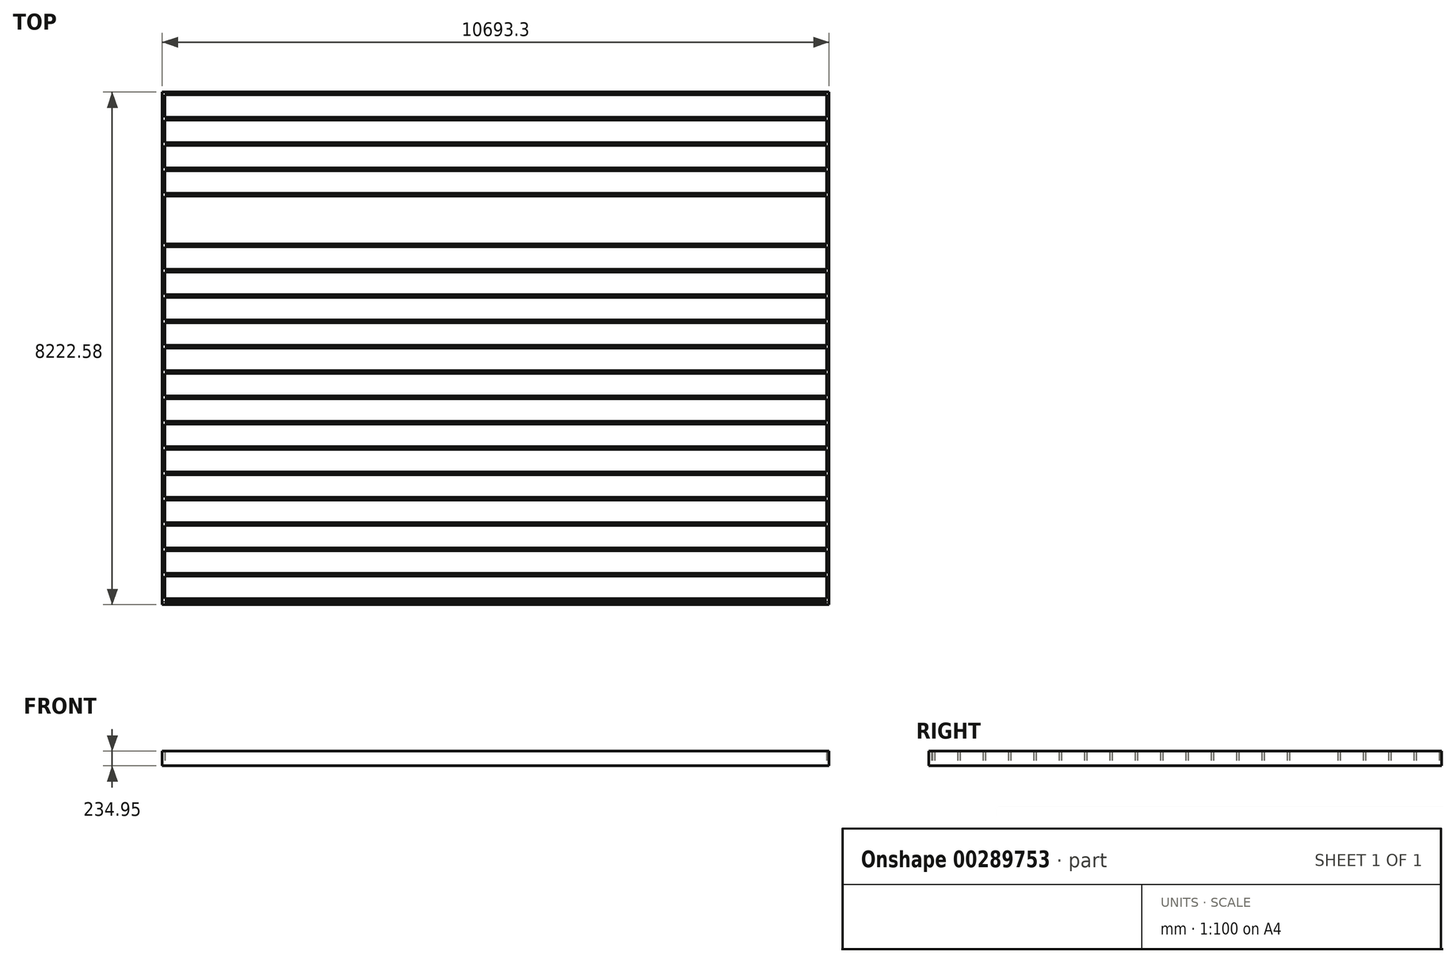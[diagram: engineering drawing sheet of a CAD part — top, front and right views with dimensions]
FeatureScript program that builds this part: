
annotation { "Feature Type Name" : "Feature", "Feature Type Description" : "" }
export const myFeature = defineFeature(function(context is Context, id is Id, definition is map)
    precondition{}
    {
        {
            var Q0;
            Q0=qCreatedBy(makeId("Top.planeOp"),FACE);
            var sketch = newSketch(context, id + "F0", { "sketchPlane" : qUnion([Q0])});
            skLineSegment(sketch, "E0.bottom", {"start": v(-5346.65, -4111.3) * mm, "end": v(5346.65, -4111.3) * mm});
            skLineSegment(sketch, "E0.top", {"start": v(-5346.65, 4111.3) * mm, "end": v(5346.65, 4111.3) * mm});
            skLineSegment(sketch, "E0.left", {"start": v(-5346.65, -4111.3) * mm, "end": v(-5346.65, 4111.3) * mm});
            skLineSegment(sketch, "E0.right", {"start": v(5346.65, -4111.3) * mm, "end": v(5346.65, 4111.3) * mm});
            skPoint(sketch, "E0.middle", {"position": v(0, 0) * mm});
            skLineSegment(sketch, "E1.bottom", {"start": v(5305.5, -4070.15) * mm, "end": v(-5305.5, -4070.15) * mm});
            skLineSegment(sketch, "E1.top", {"start": v(5305.5, 4070.15) * mm, "end": v(-5305.5, 4070.15) * mm});
            skLineSegment(sketch, "E1.left", {"start": v(5305.5, -4070.15) * mm, "end": v(5305.5, 4070.15) * mm});
            skLineSegment(sketch, "E1.right", {"start": v(-5305.5, -4070.15) * mm, "end": v(-5305.5, 4070.15) * mm});
            skLineSegment(sketch, "E2", {"start": v(-5305.5, 3704.9) * mm, "end": v(5305.5, 3704.9) * mm});
            skLineSegment(sketch, "E3", {"start": v(5305.5, 3663.75) * mm, "end": v(-5305.5, 3663.75) * mm});
            skLineSegment(sketch, "E4", {"start": v(-5305.5, 3298.5) * mm, "end": v(5305.5, 3298.5) * mm});
            skLineSegment(sketch, "E5", {"start": v(5305.5, 3257.35) * mm, "end": v(-5305.5, 3257.35) * mm});
            skLineSegment(sketch, "E6", {"start": v(-5305.5, 3277.92) * mm, "end": v(5305.5, 3277.92) * mm, "construction": true});
            skLineSegment(sketch, "E7.MirrorCS", {"start": v(5305.5, 2892.1) * mm, "end": v(-5305.5, 2892.1) * mm});
            skLineSegment(sketch, "E8.MirrorCS", {"start": v(-5305.5, 2850.95) * mm, "end": v(5305.5, 2850.95) * mm});
            skLineSegment(sketch, "E9", {"start": v(5305.5, 2871.52) * mm, "end": v(-5305.5, 2871.52) * mm, "construction": true});
            skLineSegment(sketch, "E10.MirrorCS", {"start": v(5305.5, 2485.7) * mm, "end": v(-5305.5, 2485.7) * mm});
            skLineSegment(sketch, "E11.MirrorCS", {"start": v(-5305.5, 2444.55) * mm, "end": v(5305.5, 2444.55) * mm});
            skLineSegment(sketch, "E12.MirrorCS", {"start": v(-5305.5, 2465.12) * mm, "end": v(5305.5, 2465.12) * mm, "construction": true});
            skLineSegment(sketch, "E13.MirrorCS", {"start": v(5305.5, 2079.3) * mm, "end": v(-5305.5, 2079.3) * mm});
            skLineSegment(sketch, "E14.MirrorCS", {"start": v(-5305.5, 2038.15) * mm, "end": v(5305.5, 2038.15) * mm});
            skLineSegment(sketch, "E15.MirrorCS", {"start": v(-5305.5, 2079.3) * mm, "end": v(5305.5, 2079.3) * mm});
            skLineSegment(sketch, "E16.MirrorCS", {"start": v(5305.5, 2038.15) * mm, "end": v(-5305.5, 2038.15) * mm});
            skLineSegment(sketch, "E17.MirrorCS", {"start": v(5305.5, 1672.9) * mm, "end": v(-5305.5, 1672.9) * mm});
            skLineSegment(sketch, "E18.MirrorCS", {"start": v(-5305.5, 1631.75) * mm, "end": v(5305.5, 1631.75) * mm});
            skLineSegment(sketch, "E19.MirrorCS", {"start": v(5305.5, 1266.5) * mm, "end": v(-5305.5, 1266.5) * mm});
            skLineSegment(sketch, "E20.MirrorCS", {"start": v(-5305.5, 1225.35) * mm, "end": v(5305.5, 1225.35) * mm});
            skLineSegment(sketch, "E21", {"start": v(-5305.5, 1245.92) * mm, "end": v(5305.5, 1245.92) * mm, "construction": true});
            skLineSegment(sketch, "E22.MirrorCS", {"start": v(-5305.5, 860.1) * mm, "end": v(5305.5, 860.1) * mm});
            skLineSegment(sketch, "E23.MirrorCS", {"start": v(5305.5, 818.95) * mm, "end": v(-5305.5, 818.95) * mm});
            skLineSegment(sketch, "E24.MirrorCS", {"start": v(5305.5, 453.7) * mm, "end": v(-5305.5, 453.7) * mm});
            skLineSegment(sketch, "E25.MirrorCS", {"start": v(-5305.5, 412.55) * mm, "end": v(5305.5, 412.55) * mm});
            skLineSegment(sketch, "E26.MirrorCS", {"start": v(-5305.5, 47.3) * mm, "end": v(5305.5, 47.3) * mm});
            skLineSegment(sketch, "E27.MirrorCS", {"start": v(5305.5, 6.15) * mm, "end": v(-5305.5, 6.15) * mm});
            skLineSegment(sketch, "E28.MirrorCS", {"start": v(-5305.5, -359.1) * mm, "end": v(5305.5, -359.1) * mm});
            skLineSegment(sketch, "E29.MirrorCS", {"start": v(5305.5, -400.25) * mm, "end": v(-5305.5, -400.25) * mm});
            skLineSegment(sketch, "E30.MirrorCS", {"start": v(5305.5, -765.5) * mm, "end": v(-5305.5, -765.5) * mm});
            skLineSegment(sketch, "E31.MirrorCS", {"start": v(-5305.5, -806.65) * mm, "end": v(5305.5, -806.65) * mm});
            skLineSegment(sketch, "E32.MirrorCS", {"start": v(5305.5, -1171.9) * mm, "end": v(-5305.5, -1171.9) * mm});
            skLineSegment(sketch, "E33.MirrorCS", {"start": v(-5305.5, -1213.05) * mm, "end": v(5305.5, -1213.05) * mm});
            skLineSegment(sketch, "E34", {"start": v(-5305.5, -1192.48) * mm, "end": v(5305.5, -1192.48) * mm, "construction": true});
            skLineSegment(sketch, "E35.MirrorCS", {"start": v(-5305.5, -1578.3) * mm, "end": v(5305.5, -1578.3) * mm});
            skLineSegment(sketch, "E36.MirrorCS", {"start": v(5305.5, -1619.45) * mm, "end": v(-5305.5, -1619.45) * mm});
            skLineSegment(sketch, "E37.MirrorCS", {"start": v(5305.5, -1984.7) * mm, "end": v(-5305.5, -1984.7) * mm});
            skLineSegment(sketch, "E38.MirrorCS", {"start": v(-5305.5, -2025.85) * mm, "end": v(5305.5, -2025.85) * mm});
            skLineSegment(sketch, "E39.MirrorCS", {"start": v(5305.5, -2391.1) * mm, "end": v(-5305.5, -2391.1) * mm});
            skLineSegment(sketch, "E40.MirrorCS", {"start": v(-5305.5, -2432.25) * mm, "end": v(5305.5, -2432.25) * mm});
            skLineSegment(sketch, "E41.MirrorCS", {"start": v(-5305.5, -2797.5) * mm, "end": v(5305.5, -2797.5) * mm});
            skLineSegment(sketch, "E42.MirrorCS", {"start": v(5305.5, -2838.65) * mm, "end": v(-5305.5, -2838.65) * mm});
            skLineSegment(sketch, "E43.MirrorCS", {"start": v(5305.5, -3203.9) * mm, "end": v(-5305.5, -3203.9) * mm});
            skLineSegment(sketch, "E44.MirrorCS", {"start": v(-5305.5, -3245.05) * mm, "end": v(5305.5, -3245.05) * mm});
            skLineSegment(sketch, "E45.MirrorCS", {"start": v(-5305.5, -3610.3) * mm, "end": v(5305.5, -3610.3) * mm});
            skLineSegment(sketch, "E46.MirrorCS", {"start": v(5305.5, -3651.45) * mm, "end": v(-5305.5, -3651.45) * mm});
            skLineSegment(sketch, "E47.MirrorCS", {"start": v(-5305.5, -4016.7) * mm, "end": v(5305.5, -4016.7) * mm});
            skLineSegment(sketch, "E48.MirrorCS", {"start": v(5305.5, -4057.85) * mm, "end": v(-5305.5, -4057.85) * mm});
            skLineSegment(sketch, "E49.MirrorCS", {"start": v(5305.5, -5277.05) * mm, "end": v(-5305.5, -5277.05) * mm});
            skLineSegment(sketch, "E50.MirrorCS", {"start": v(-5305.5, -5235.9) * mm, "end": v(5305.5, -5235.9) * mm});
            skLineSegment(sketch, "E51.MirrorCS", {"start": v(5305.5, -4870.65) * mm, "end": v(-5305.5, -4870.65) * mm});
            skLineSegment(sketch, "E52.MirrorCS", {"start": v(-5305.5, -4829.5) * mm, "end": v(5305.5, -4829.5) * mm});
            skLineSegment(sketch, "E53.MirrorCS", {"start": v(-5305.5, -4464.25) * mm, "end": v(5305.5, -4464.25) * mm});
            skLineSegment(sketch, "E54.MirrorCS", {"start": v(5305.5, -4423.1) * mm, "end": v(-5305.5, -4423.1) * mm});
            skSolve(sketch);
        }
        {
            var Q0;
            Q0=makeQuery(id+"F0.imprint","IMPRINT",FACE,{"disambiguationData":[TD([[makeQuery(id+"F0.imprint","IMPRINT",EDGE,{"derivedFrom":sQuery(id+"F0.wireOp",EDGE,"E0.bottom")}),1.0]])]});
            var Q1;
            {var subQ0=sQuery(id+"F0.wireOp",EDGE,"E2");Q1=makeQuery(id+"F0.imprint","IMPRINT",FACE,{"disambiguationData":[TD([[makeQuery(id+"F0.imprint","IMPRINT",EDGE,{"derivedFrom":subQ0}),-1.0]])]});}
            var Q2;
            {var subQ0=sQuery(id+"F0.wireOp",EDGE,"E4");Q2=makeQuery(id+"F0.imprint","IMPRINT",FACE,{"disambiguationData":[TD([[makeQuery(id+"F0.imprint","IMPRINT",EDGE,{"derivedFrom":subQ0}),-1.0]])]});}
            var Q3;
            {var subQ0=sQuery(id+"F0.wireOp",EDGE,"E7.MirrorCS");Q3=makeQuery(id+"F0.imprint","IMPRINT",FACE,{"disambiguationData":[TD([[makeQuery(id+"F0.imprint","IMPRINT",EDGE,{"derivedFrom":subQ0}),1.0]])]});}
            var Q4;
            {var subQ0=sQuery(id+"F0.wireOp",EDGE,"E10.MirrorCS");Q4=makeQuery(id+"F0.imprint","IMPRINT",FACE,{"disambiguationData":[TD([[makeQuery(id+"F0.imprint","IMPRINT",EDGE,{"derivedFrom":subQ0}),1.0]])]});}
            var Q5;
            {var subQ0=sQuery(id+"F0.wireOp",EDGE,"E15.MirrorCS");Q5=makeQuery(id+"F0.imprint","IMPRINT",FACE,{"disambiguationData":[TD([[makeQuery(id+"F0.imprint","IMPRINT",EDGE,{"derivedFrom":subQ0}),-1.0]])]});}
            var Q6;
            {var subQ0=sQuery(id+"F0.wireOp",EDGE,"E17.MirrorCS");Q6=makeQuery(id+"F0.imprint","IMPRINT",FACE,{"disambiguationData":[TD([[makeQuery(id+"F0.imprint","IMPRINT",EDGE,{"derivedFrom":subQ0}),1.0]])]});}
            var Q7;
            {var subQ0=sQuery(id+"F0.wireOp",EDGE,"E19.MirrorCS");Q7=makeQuery(id+"F0.imprint","IMPRINT",FACE,{"disambiguationData":[TD([[makeQuery(id+"F0.imprint","IMPRINT",EDGE,{"derivedFrom":subQ0}),1.0]])]});}
            var Q8;
            {var subQ0=sQuery(id+"F0.wireOp",EDGE,"E22.MirrorCS");Q8=makeQuery(id+"F0.imprint","IMPRINT",FACE,{"disambiguationData":[TD([[makeQuery(id+"F0.imprint","IMPRINT",EDGE,{"derivedFrom":subQ0}),-1.0]])]});}
            var Q9;
            {var subQ0=sQuery(id+"F0.wireOp",EDGE,"E24.MirrorCS");Q9=makeQuery(id+"F0.imprint","IMPRINT",FACE,{"disambiguationData":[TD([[makeQuery(id+"F0.imprint","IMPRINT",EDGE,{"derivedFrom":subQ0}),1.0]])]});}
            var Q10;
            {var subQ0=sQuery(id+"F0.wireOp",EDGE,"E26.MirrorCS");Q10=makeQuery(id+"F0.imprint","IMPRINT",FACE,{"disambiguationData":[TD([[makeQuery(id+"F0.imprint","IMPRINT",EDGE,{"derivedFrom":subQ0}),-1.0]])]});}
            var Q11;
            {var subQ0=sQuery(id+"F0.wireOp",EDGE,"E28.MirrorCS");Q11=makeQuery(id+"F0.imprint","IMPRINT",FACE,{"disambiguationData":[TD([[makeQuery(id+"F0.imprint","IMPRINT",EDGE,{"derivedFrom":subQ0}),-1.0]])]});}
            var Q12;
            {var subQ0=sQuery(id+"F0.wireOp",EDGE,"E30.MirrorCS");Q12=makeQuery(id+"F0.imprint","IMPRINT",FACE,{"disambiguationData":[TD([[makeQuery(id+"F0.imprint","IMPRINT",EDGE,{"derivedFrom":subQ0}),1.0]])]});}
            var Q13;
            {var subQ0=sQuery(id+"F0.wireOp",EDGE,"E32.MirrorCS");Q13=makeQuery(id+"F0.imprint","IMPRINT",FACE,{"disambiguationData":[TD([[makeQuery(id+"F0.imprint","IMPRINT",EDGE,{"derivedFrom":subQ0}),1.0]])]});}
            var Q14;
            {var subQ0=sQuery(id+"F0.wireOp",EDGE,"E35.MirrorCS");Q14=makeQuery(id+"F0.imprint","IMPRINT",FACE,{"disambiguationData":[TD([[makeQuery(id+"F0.imprint","IMPRINT",EDGE,{"derivedFrom":subQ0}),-1.0]])]});}
            var Q15;
            {var subQ0=sQuery(id+"F0.wireOp",EDGE,"E37.MirrorCS");Q15=makeQuery(id+"F0.imprint","IMPRINT",FACE,{"disambiguationData":[TD([[makeQuery(id+"F0.imprint","IMPRINT",EDGE,{"derivedFrom":subQ0}),1.0]])]});}
            var Q16;
            {var subQ0=sQuery(id+"F0.wireOp",EDGE,"E39.MirrorCS");Q16=makeQuery(id+"F0.imprint","IMPRINT",FACE,{"disambiguationData":[TD([[makeQuery(id+"F0.imprint","IMPRINT",EDGE,{"derivedFrom":subQ0}),1.0]])]});}
            var Q17;
            {var subQ0=sQuery(id+"F0.wireOp",EDGE,"E41.MirrorCS");Q17=makeQuery(id+"F0.imprint","IMPRINT",FACE,{"disambiguationData":[TD([[makeQuery(id+"F0.imprint","IMPRINT",EDGE,{"derivedFrom":subQ0}),-1.0]])]});}
            var Q18;
            {var subQ0=sQuery(id+"F0.wireOp",EDGE,"E43.MirrorCS");Q18=makeQuery(id+"F0.imprint","IMPRINT",FACE,{"disambiguationData":[TD([[makeQuery(id+"F0.imprint","IMPRINT",EDGE,{"derivedFrom":subQ0}),1.0]])]});}
            var Q19;
            {var subQ0=sQuery(id+"F0.wireOp",EDGE,"E45.MirrorCS");Q19=makeQuery(id+"F0.imprint","IMPRINT",FACE,{"disambiguationData":[TD([[makeQuery(id+"F0.imprint","IMPRINT",EDGE,{"derivedFrom":subQ0}),-1.0]])]});}
            var Q20;
            {var subQ0=sQuery(id+"F0.wireOp",EDGE,"E47.MirrorCS");Q20=makeQuery(id+"F0.imprint","IMPRINT",FACE,{"disambiguationData":[TD([[makeQuery(id+"F0.imprint","IMPRINT",EDGE,{"derivedFrom":subQ0}),-1.0]])]});}
            var Q21;
            {var subQ0=sQuery(id+"F0.wireOp",EDGE,"E53.MirrorCS");Q21=makeQuery(id+"F0.imprint","IMPRINT",FACE,{"disambiguationData":[TD([[makeQuery(id+"F0.imprint","IMPRINT",EDGE,{"derivedFrom":subQ0}),1.0]])]});}
            var Q22;
            {var subQ0=sQuery(id+"F0.wireOp",EDGE,"E51.MirrorCS");Q22=makeQuery(id+"F0.imprint","IMPRINT",FACE,{"disambiguationData":[TD([[makeQuery(id+"F0.imprint","IMPRINT",EDGE,{"derivedFrom":subQ0}),-1.0]])]});}
            var Q23;
            {var subQ0=sQuery(id+"F0.wireOp",EDGE,"E49.MirrorCS");Q23=makeQuery(id+"F0.imprint","IMPRINT",FACE,{"disambiguationData":[TD([[makeQuery(id+"F0.imprint","IMPRINT",EDGE,{"derivedFrom":subQ0}),-1.0]])]});}
            extrude(context, id + "F1", {"entities" : qUnion([Q0, Q1, Q2, Q3, Q4, Q5, Q6, Q7, Q8, Q9, Q10, Q11, Q12, Q13, Q14, Q15, Q16, Q17, Q18, Q19, Q20, Q21, Q22, Q23]), "depth" : 234.95 * mm});
        }
    });
